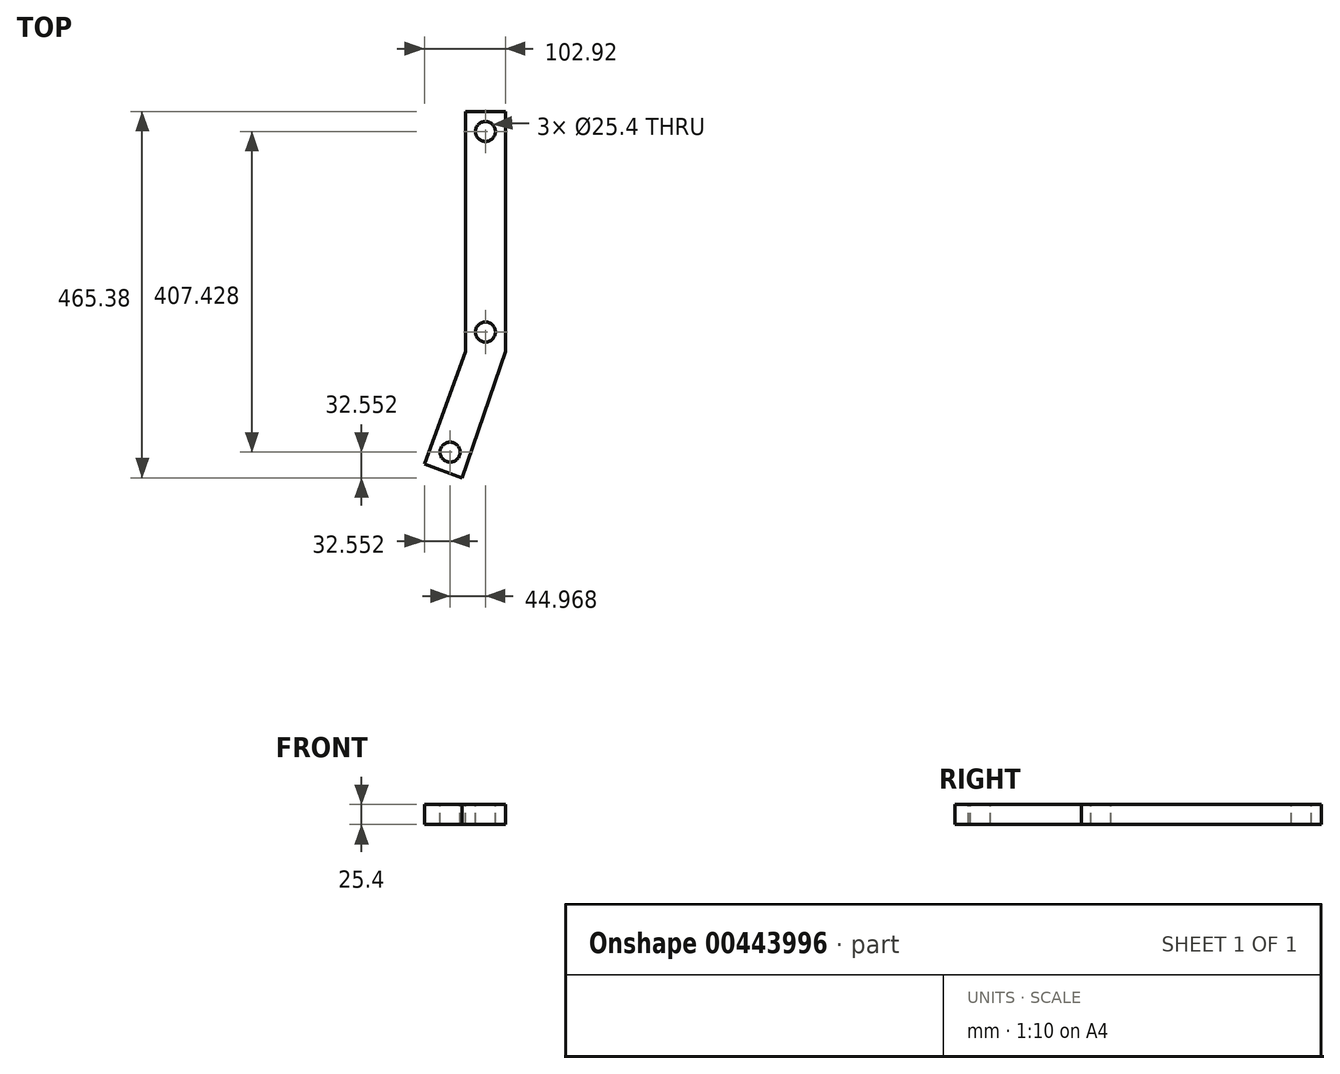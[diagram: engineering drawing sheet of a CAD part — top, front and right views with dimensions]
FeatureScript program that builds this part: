
annotation { "Feature Type Name" : "Feature", "Feature Type Description" : "" }
export const myFeature = defineFeature(function(context is Context, id is Id, definition is map)
    precondition{}
    {
        {
            var Q0;
            Q0=qCreatedBy(makeId("Front.planeOp"),FACE);
            var sketch = newSketch(context, id + "F0", { "sketchPlane" : qUnion([Q0])});
            skLineSegment(sketch, "E0.bottom", {"start": v(0, 0) * mm, "end": v(-50.8, 0) * mm});
            skLineSegment(sketch, "E0.top", {"start": v(0, 25.4) * mm, "end": v(-50.8, 25.4) * mm});
            skLineSegment(sketch, "E0.left", {"start": v(0, 0) * mm, "end": v(0, 25.4) * mm});
            skLineSegment(sketch, "E0.right", {"start": v(-50.8, 0) * mm, "end": v(-50.8, 25.4) * mm});
            skSolve(sketch);
        }
        {
            var Q0;
            Q0=makeQuery(id+"F0.imprint","IMPRINT",FACE,{"disambiguationData":[TD([[makeQuery(id+"F0.imprint","IMPRINT",EDGE,{"derivedFrom":sQuery(id+"F0.wireOp",EDGE,"E0.bottom")}),-1.0]])]});
            extrude(context, id + "F1", {"entities" : qUnion([Q0]), "depth" : 304.8 * mm});
        }
        {
            var Q0;
            Q0=makeQuery(id+"F1.opExtrude","SWEPT_FACE",FACE,{"disambiguationData":[OSD([sQuery(id+"F0.wireOp",EDGE,"E0.top")])]});
            var sketch = newSketch(context, id + "F2", { "sketchPlane" : qUnion([Q0])});
            skLineSegment(sketch, "E1", {"start": v(-50.8, -304.8) * mm, "end": v(-102.92, -448) * mm});
            skLineSegment(sketch, "E2", {"start": v(-102.92, -448) * mm, "end": v(-55.19, -465.38) * mm});
            skLineSegment(sketch, "E3", {"start": v(-55.19, -465.38) * mm, "end": v(0, -304.8) * mm});
            skSolve(sketch);
        }
        {
            var Q0;
            Q0=makeQuery(id+"F2.imprint","IMPRINT",FACE,{"disambiguationData":[TD([[makeQuery(id+"F2.imprint","IMPRINT",EDGE,{"derivedFrom":sQuery(id+"F2.wireOp",EDGE,"E1")}),1.0]])]});
            extrude(context, id + "F3", {"entities" : qUnion([Q0]), "operationType" : NewBodyOperationType.ADD, "oppositeDirection" : true, "depth" : 25.4 * mm});
        }
        {
            var Q0;
            {var subQ0=sQuery(id+"F0.wireOp",EDGE,"E0.top");Q0=makeQuery(id+"F3.boolean.opBoolean","MERGE",FACE,{"derivedFrom":[makeQuery(id+"F1.opExtrude","SWEPT_FACE",FACE,{"disambiguationData":[OSD([subQ0])]}),makeQuery(id+"F3.opExtrude","CAP_FACE",FACE,{"disambiguationData":[OSD([subQ0,sQuery(id+"F2.wireOp",EDGE,"E1"),sQuery(id+"F2.wireOp",EDGE,"E2"),sQuery(id+"F2.wireOp",EDGE,"E3")])],"isStart":true})]});}
            var sketch = newSketch(context, id + "F4", { "sketchPlane" : qUnion([Q0])});
            skCircle(sketch, "E4", {"center": v(-25.4, -25.4) * mm, "radius": 12.7 * mm});
            skSolve(sketch);
        }
        {
            var Q0;
            Q0=makeQuery(id+"F4.imprint","IMPRINT",FACE,{"disambiguationData":[TD([[makeQuery(id+"F4.imprint","IMPRINT",EDGE,{"derivedFrom":sQuery(id+"F4.wireOp",EDGE,"E4")}),1.0]])]});
            extrude(context, id + "F5", {"entities" : qUnion([Q0]), "operationType" : NewBodyOperationType.REMOVE, "oppositeDirection" : true, "depth" : 25.4 * mm});
        }
        {
            var Q0;
            {var subQ0=sQuery(id+"F0.wireOp",EDGE,"E0.top");Q0=makeQuery(id+"F3.boolean.opBoolean","MERGE",FACE,{"derivedFrom":[makeQuery(id+"F1.opExtrude","SWEPT_FACE",FACE,{"disambiguationData":[OSD([subQ0])]}),makeQuery(id+"F3.opExtrude","CAP_FACE",FACE,{"disambiguationData":[OSD([subQ0,sQuery(id+"F2.wireOp",EDGE,"E1"),sQuery(id+"F2.wireOp",EDGE,"E2"),sQuery(id+"F2.wireOp",EDGE,"E3")])],"isStart":true})]});}
            var sketch = newSketch(context, id + "F6", { "sketchPlane" : qUnion([Q0])});
            skCircle(sketch, "E5", {"center": v(-70.37, -432.83) * mm, "radius": 12.7 * mm});
            skSolve(sketch);
        }
        {
            var Q0;
            Q0=makeQuery(id+"F6.imprint","IMPRINT",FACE,{"disambiguationData":[TD([[makeQuery(id+"F6.imprint","IMPRINT",EDGE,{"derivedFrom":sQuery(id+"F6.wireOp",EDGE,"E5")}),1.0]])]});
            extrude(context, id + "F7", {"entities" : qUnion([Q0]), "operationType" : NewBodyOperationType.REMOVE, "oppositeDirection" : true, "depth" : 25.4 * mm});
        }
        {
            var Q0;
            {var subQ0=sQuery(id+"F0.wireOp",EDGE,"E0.top");Q0=makeQuery(id+"F3.boolean.opBoolean","MERGE",FACE,{"derivedFrom":[makeQuery(id+"F1.opExtrude","SWEPT_FACE",FACE,{"disambiguationData":[OSD([subQ0])]}),makeQuery(id+"F3.opExtrude","CAP_FACE",FACE,{"disambiguationData":[OSD([subQ0,sQuery(id+"F2.wireOp",EDGE,"E1"),sQuery(id+"F2.wireOp",EDGE,"E2"),sQuery(id+"F2.wireOp",EDGE,"E3")])],"isStart":true})]});}
            var sketch = newSketch(context, id + "F8", { "sketchPlane" : qUnion([Q0])});
            skCircle(sketch, "E6", {"center": v(-25.4, -280.16) * mm, "radius": 12.7 * mm});
            skSolve(sketch);
        }
        {
            var Q0;
            Q0=makeQuery(id+"F8.imprint","IMPRINT",FACE,{"disambiguationData":[TD([[makeQuery(id+"F8.imprint","IMPRINT",EDGE,{"derivedFrom":sQuery(id+"F8.wireOp",EDGE,"E6")}),1.0]])]});
            extrude(context, id + "F9", {"entities" : qUnion([Q0]), "operationType" : NewBodyOperationType.REMOVE, "oppositeDirection" : true, "depth" : 25.4 * mm});
        }
    });
